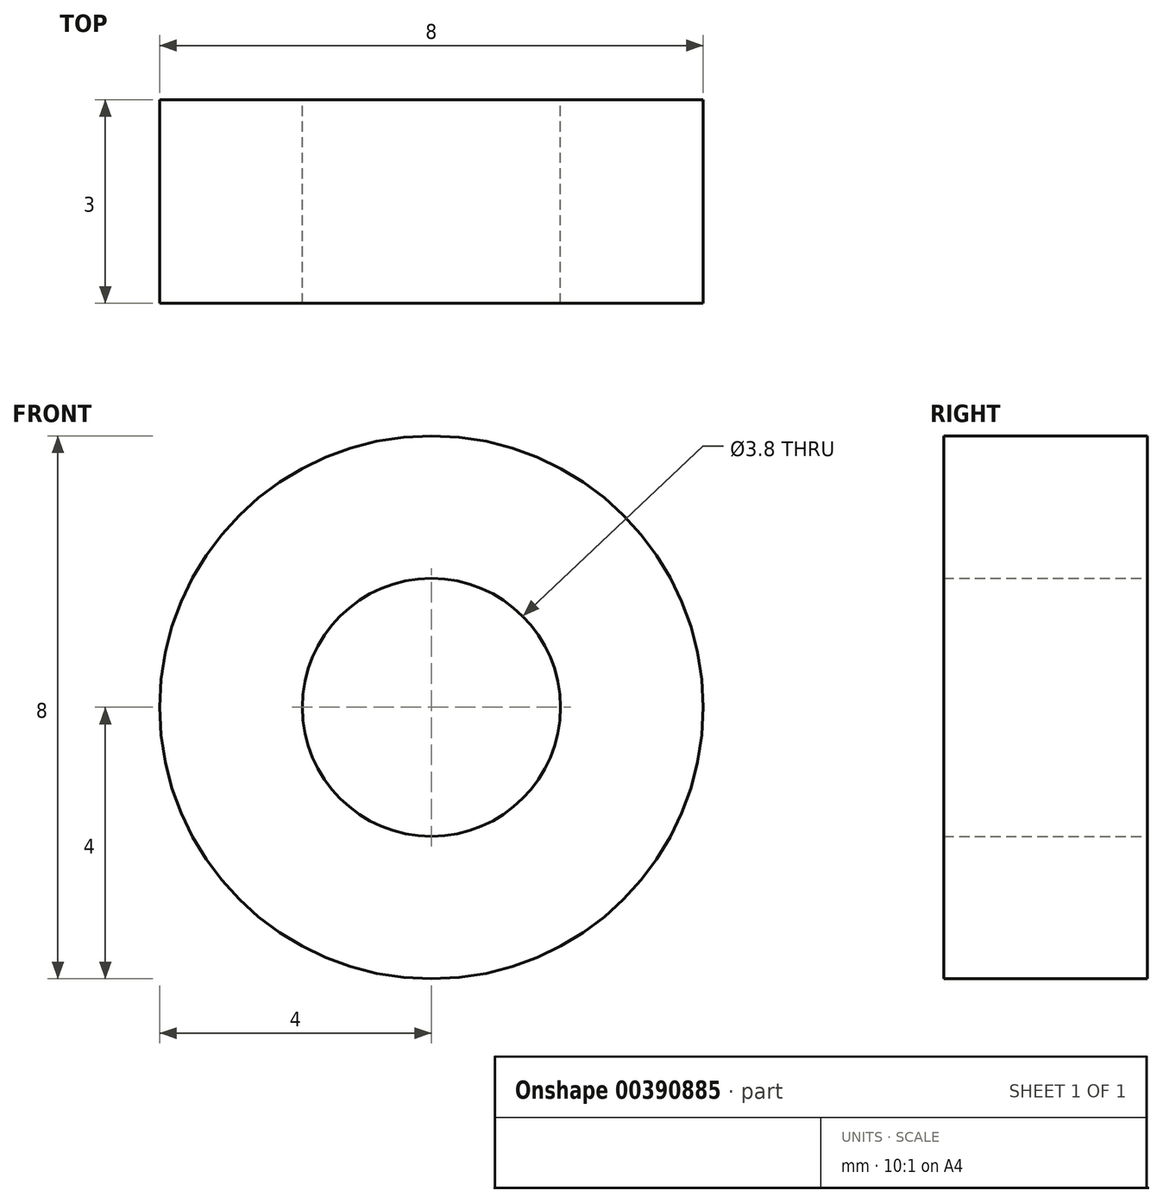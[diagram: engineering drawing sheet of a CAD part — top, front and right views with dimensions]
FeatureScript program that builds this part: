
annotation { "Feature Type Name" : "Feature", "Feature Type Description" : "" }
export const myFeature = defineFeature(function(context is Context, id is Id, definition is map)
    precondition{}
    {
        {
            var Q0;
            Q0=qCreatedBy(makeId("Front.planeOp"),FACE);
            var sketch = newSketch(context, id + "F0", { "sketchPlane" : qUnion([Q0])});
            skCircle(sketch, "E0", {"center": v(0, 0) * mm, "radius": 4 * mm});
            skCircle(sketch, "E1", {"center": v(0, 0) * mm, "radius": 1.9 * mm});
            skSolve(sketch);
        }
        {
            var Q0;
            Q0=makeQuery(id+"F0.imprint","IMPRINT",FACE,{"disambiguationData":[TD([[makeQuery(id+"F0.imprint","IMPRINT",EDGE,{"derivedFrom":sQuery(id+"F0.wireOp",EDGE,"E0")}),1.0]])]});
            extrude(context, id + "F1", {"entities" : qUnion([Q0]), "endBound" : BoundingType.SYMMETRIC, "depth" : 3 * mm});
        }
    });
